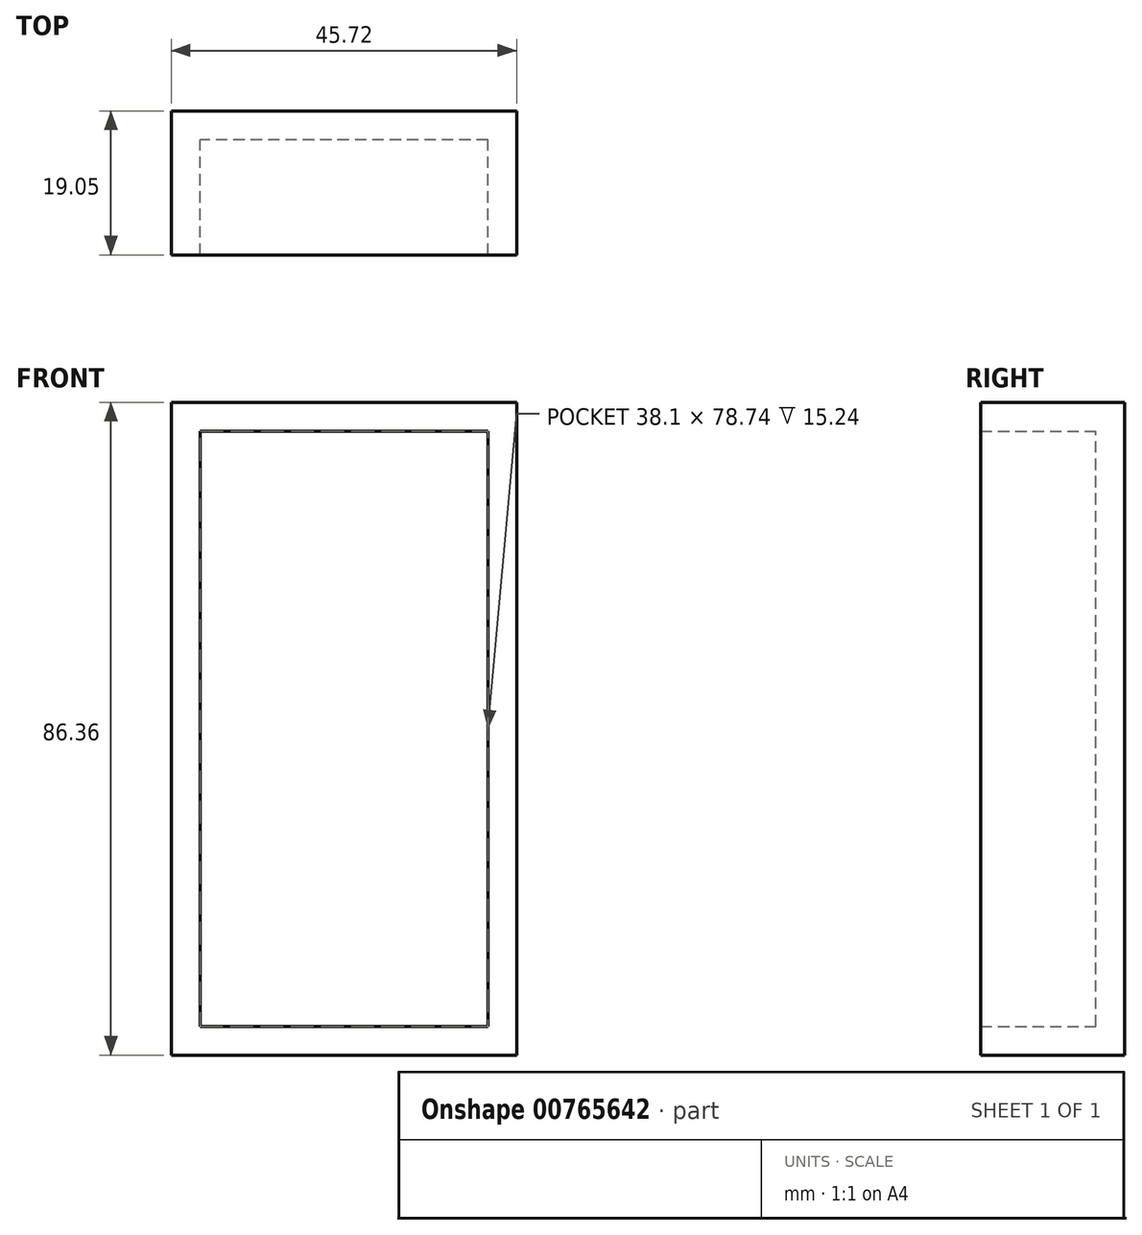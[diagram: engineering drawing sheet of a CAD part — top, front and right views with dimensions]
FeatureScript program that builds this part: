
annotation { "Feature Type Name" : "Feature", "Feature Type Description" : "" }
export const myFeature = defineFeature(function(context is Context, id is Id, definition is map)
    precondition{}
    {
        {
            var Q0;
            Q0=qCreatedBy(makeId("Front.planeOp"),FACE);
            var sketch = newSketch(context, id + "F0", { "sketchPlane" : qUnion([Q0])});
            skLineSegment(sketch, "E0", {"start": v(0, 0) * mm, "end": v(0, 86.36) * mm});
            skLineSegment(sketch, "E1", {"start": v(0, 86.36) * mm, "end": v(45.72, 86.36) * mm});
            skLineSegment(sketch, "E2", {"start": v(45.72, 86.36) * mm, "end": v(45.72, 0) * mm});
            skLineSegment(sketch, "E3", {"start": v(45.72, 0) * mm, "end": v(0, 0) * mm});
            skSolve(sketch);
        }
        {
            var Q0;
            Q0=makeQuery(id+"F0.imprint","IMPRINT",FACE,{"disambiguationData":[TD([[makeQuery(id+"F0.imprint","IMPRINT",EDGE,{"derivedFrom":sQuery(id+"F0.wireOp",EDGE,"E0")}),-1.0]])]});
            extrude(context, id + "F1", {"entities" : qUnion([Q0]), "depth" : 19.05 * mm, "offsetDistance" : 25.4 * mm});
        }
        {
            var Q0;
            Q0=makeQuery(id+"F1.opExtrude","CAP_FACE",FACE,{"disambiguationData":[OSD([sQuery(id+"F0.wireOp",EDGE,"E0"),sQuery(id+"F0.wireOp",EDGE,"E1"),sQuery(id+"F0.wireOp",EDGE,"E2"),sQuery(id+"F0.wireOp",EDGE,"E3")])],"isStart":false});
            shell(context, id + "F2", {"entities" : qUnion([Q0]), "thickness" : 3.8 * mm});
        }
    });
